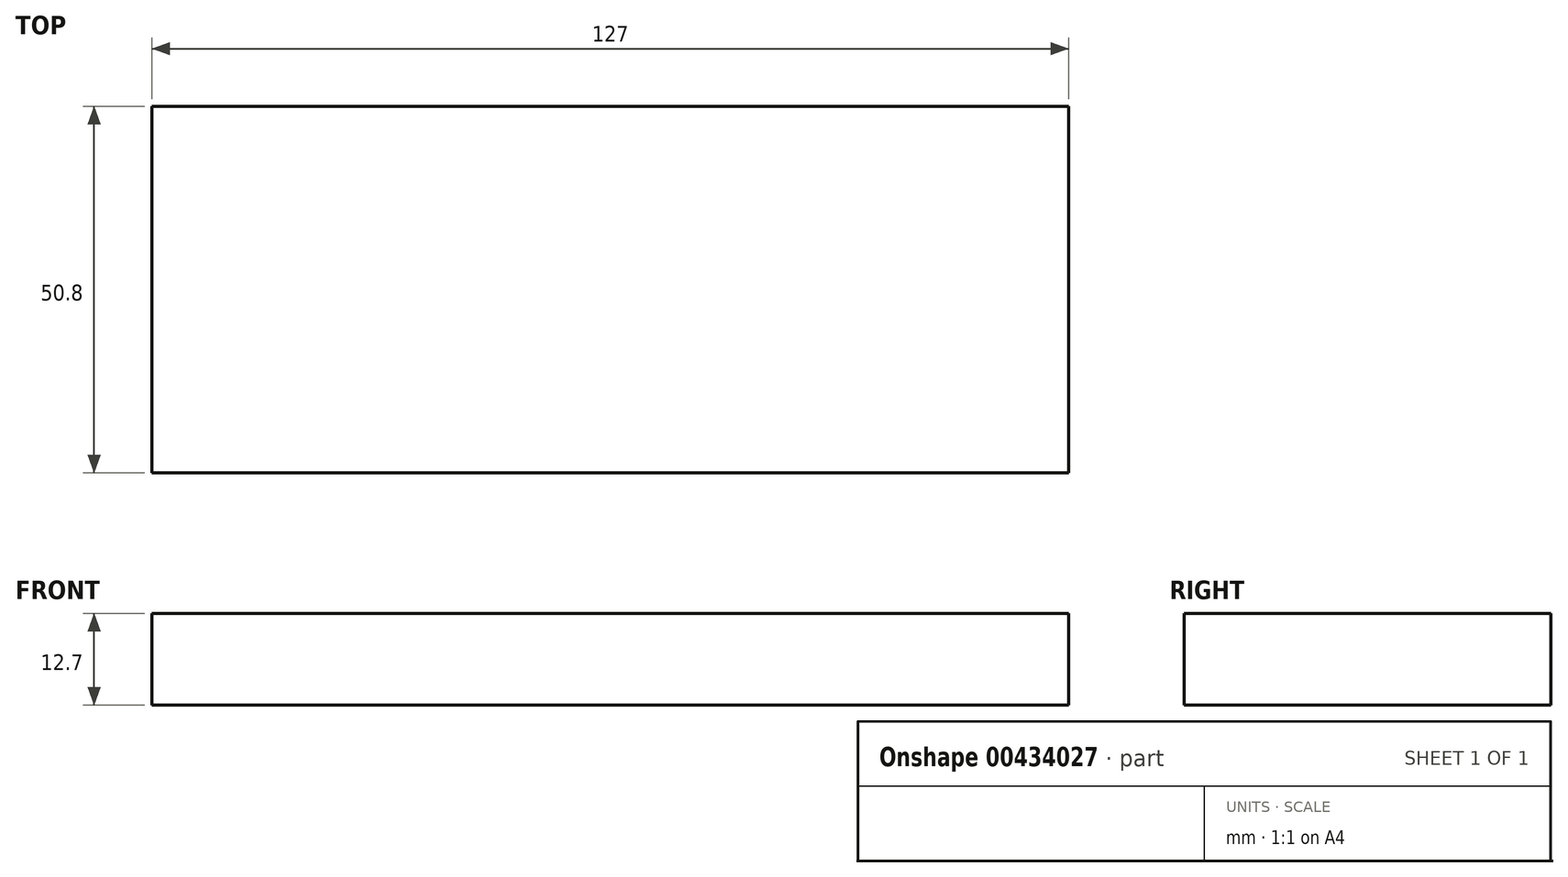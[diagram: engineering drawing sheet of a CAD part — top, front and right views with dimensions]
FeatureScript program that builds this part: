
annotation { "Feature Type Name" : "Feature", "Feature Type Description" : "" }
export const myFeature = defineFeature(function(context is Context, id is Id, definition is map)
    precondition{}
    {
        {
            var Q0;
            Q0=qCreatedBy(makeId("Top.planeOp"),FACE);
            var sketch = newSketch(context, id + "F0", { "sketchPlane" : qUnion([Q0])});
            skLineSegment(sketch, "E0.bottom", {"start": v(0, 0) * mm, "end": v(127, 0) * mm});
            skLineSegment(sketch, "E0.top", {"start": v(0, -50.8) * mm, "end": v(127, -50.8) * mm});
            skLineSegment(sketch, "E0.left", {"start": v(0, 0) * mm, "end": v(0, -50.8) * mm});
            skLineSegment(sketch, "E0.right", {"start": v(127, 0) * mm, "end": v(127, -50.8) * mm});
            skSolve(sketch);
        }
        {
            var Q0;
            Q0 = qSketchRegion(id + "F0", true);
            extrude(context, id + "F1", {"entities" : qUnion([Q0]), "depth" : 12.7 * mm});
        }
    });
